# Revit family: DLB070002
name_source: partatom
category: Appareils sanitaires
revit_build: Autodesk Revit 2015 (Build: 20140606_1530(x64)
units: mm (PartAtom-declared; Revit-internal decimal feet)

## types (1)
- Type 1
    Category = Wash troughs
    Commentaires du type = Wall-mounted wash trough
    Description = French manufacturer Delabie is a leader in the European sanitary ware market for non-domestic places. Water controls, solutions for disabled people, sanitary ware, for schools, leisure centres, offices, hospitals, airports…
    Fabricant = DELABIE
    Features  = Wall-mounted wash trough for 2 services.
Bacteriostatic 304 stainless steel.
Stainless steel thickness: 1mm for the bowl, 1.5mm for surround and fixing brackets.
Easy to install: no joint concealers to install, lightweight wash trough.
Drainage on the right.
Supplied with 1½" waste.
Without overflow.
Supplied with brackets and fixing elements.
CE marked. Complies with European standard EN 14296.
Weight: 8.4kg.
Option to add a bacteriostatic 304 stainless steel splashback, stainless steel thickness 1.2mm.
    Finish = Polished satin
    Grade = CE
    ManufacturerName = DELABIE
    ManufacturerURL = http://www.delabie.com
    Material = 304 stainless steel
    ModelNumber = 120250
    Modèle = CANAL wash trough
    Name = CANAL wash trough
    NominalHeight = 180 mm  [stored 0.590551 ft]
    NominalLength = 1200 mm
    NominalWidth = 400 mm  [stored 1.31234 ft]
    ProductInformation = http://www.delabie.com
    Radius = 24 mm
    SerialNumber = 3456330153393
    URL = http://www.delabie.com
    Version = v1
    WarrantyDescription = Any manufacturing defect
    WarrantyDurationUnit = 10 years
    Weight = 8.4kg

note: [stored X ft] marks values corroborated as IEEE doubles in the binary element streams (Revit-internal decimal feet)

## geometry (parser evidence)
native form markers: Blend x10, Sweep x4
no freeform markers — native parametric forms only
